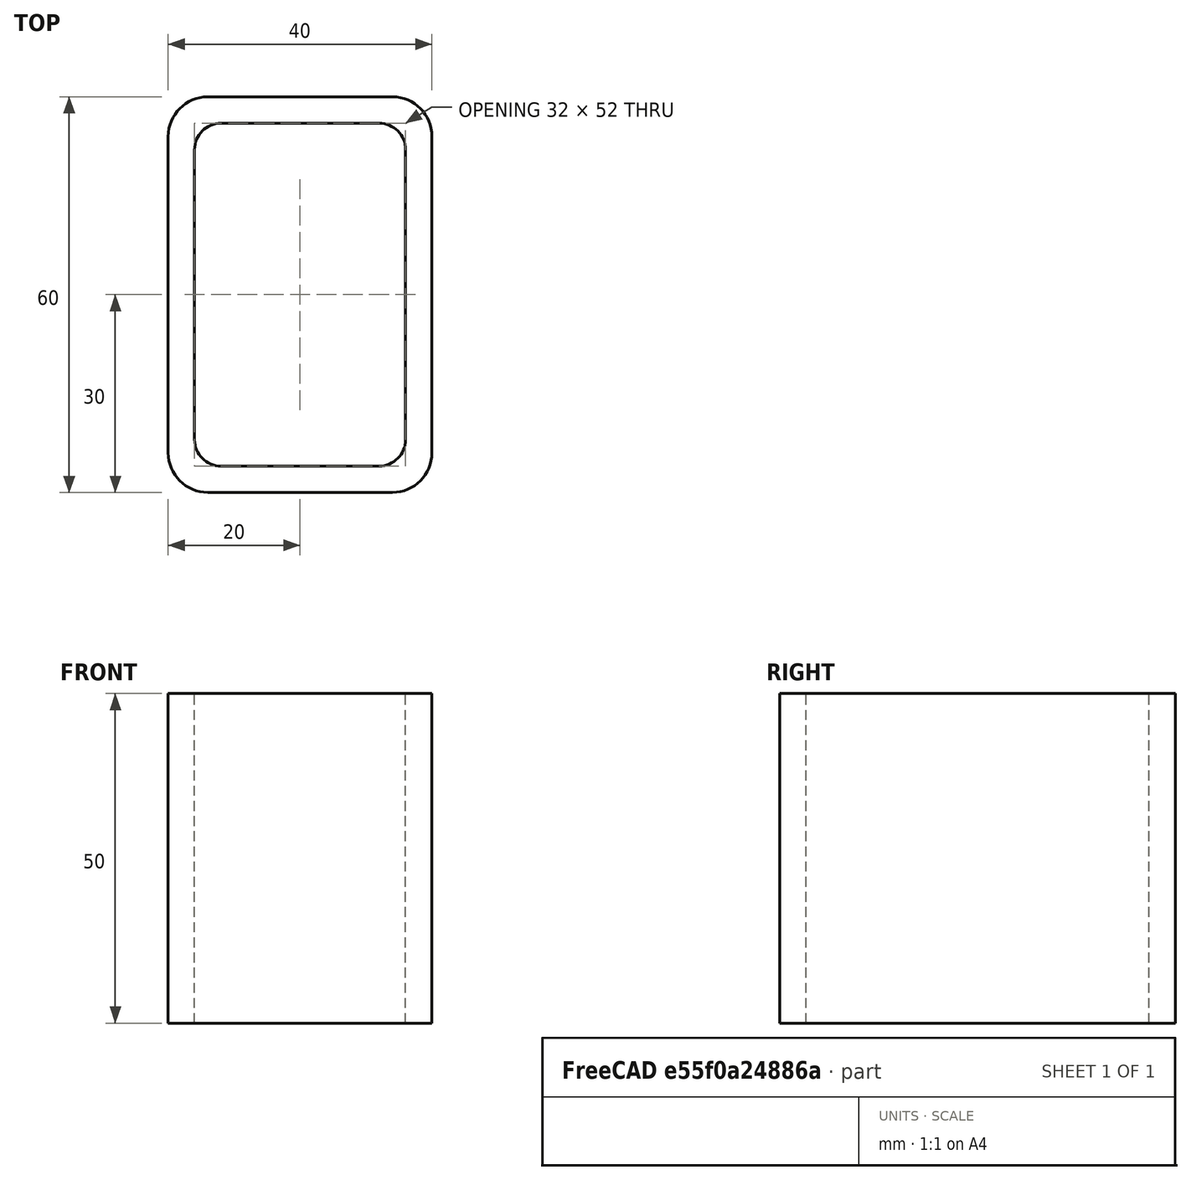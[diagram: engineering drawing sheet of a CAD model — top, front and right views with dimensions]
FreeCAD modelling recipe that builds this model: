
FCSTD DOCUMENT  (FreeCAD 0.15R4671 (Git))
Label: Rectangular hollow section 60x40x4 EN10219 S235JRH
License: All rights reserved
LicenseURL: http://en.wikipedia.org/wiki/All_rights_reserved
objects: Sketcher::SketchObject×1, Part::Extrusion×1
note: 2 computed .brp shape members not serialized (recipe doc carries the construction recipe); baked Part::Feature solids carry a one-line shape summary decoded from their .brp

FEATURE [Sketcher::SketchObject] Sketch
  sketch-geometry (16):
    g0: LineSegment StartX=-12 StartY=26 StartZ=0 EndX=12 EndY=26 EndZ=0
    g1: LineSegment StartX=16 StartY=22 StartZ=0 EndX=16 EndY=-22 EndZ=0
    g2: LineSegment StartX=12 StartY=-26 StartZ=0 EndX=-12 EndY=-26 EndZ=0
    g3: LineSegment StartX=-16 StartY=-22 StartZ=0 EndX=-16 EndY=22 EndZ=0
    g4: LineSegment StartX=-14 StartY=30 StartZ=0 EndX=14 EndY=30 EndZ=0
    g5: LineSegment StartX=20 StartY=24 StartZ=0 EndX=20 EndY=-24 EndZ=0
    g6: LineSegment StartX=14 StartY=-30 StartZ=0 EndX=-14 EndY=-30 EndZ=0
    g7: LineSegment StartX=-20 StartY=-24 StartZ=0 EndX=-20 EndY=24 EndZ=0
    g8: ArcOfCircle CenterX=-12 CenterY=22 CenterZ=0 NormalX=0 NormalY=0 NormalZ=1 Radius=4 StartAngle=1.5708 EndAngle=3.14159
    g9: ArcOfCircle CenterX=12 CenterY=22 CenterZ=0 NormalX=0 NormalY=0 NormalZ=1 Radius=4 StartAngle=0 EndAngle=1.5708
    g10: ArcOfCircle CenterX=12 CenterY=-22 CenterZ=0 NormalX=0 NormalY=0 NormalZ=1 Radius=4 StartAngle=4.71239 EndAngle=6.28319
    g11: ArcOfCircle CenterX=-12 CenterY=-22 CenterZ=0 NormalX=0 NormalY=0 NormalZ=1 Radius=4 StartAngle=3.14159 EndAngle=4.71239
    g12: ArcOfCircle CenterX=14 CenterY=24 CenterZ=0 NormalX=0 NormalY=0 NormalZ=1 Radius=6 StartAngle=0 EndAngle=1.5708
    g13: ArcOfCircle CenterX=14 CenterY=-24 CenterZ=0 NormalX=0 NormalY=0 NormalZ=1 Radius=6 StartAngle=4.71239 EndAngle=6.28319
    g14: ArcOfCircle CenterX=-14 CenterY=-24 CenterZ=0 NormalX=0 NormalY=0 NormalZ=1 Radius=6 StartAngle=3.14159 EndAngle=4.71239
    g15: ArcOfCircle CenterX=-14 CenterY=24 CenterZ=0 NormalX=0 NormalY=0 NormalZ=1 Radius=6 StartAngle=1.5708 EndAngle=3.14159
  constraints (36):
    c: Horizontal(g2)
    c: Vertical(g3)
    c: Horizontal(g6)
    c: Vertical(g7)
    c: Tangent(g3,g8) = 1.5708
    c: Tangent(g0,g8) = 1.5708
    c: Tangent(g0,g9) = 1.5708
    c: Tangent(g1,g9) = 1.5708
    c: Tangent(g1,g10) = 1.5708
    c: Tangent(g2,g10) = 1.5708
    c: Tangent(g2,g11) = 1.5708
    c: Tangent(g3,g11) = 1.5708
    c: Tangent(g4,g12) = 1.5708
    c: Tangent(g5,g12) = 1.5708
    c: Tangent(g5,g13) = 1.5708
    c: Tangent(g6,g13) = 1.5708
    c: Tangent(g6,g14) = 1.5708
    c: Tangent(g7,g14) = 1.5708
    c: Tangent(g7,g15) = 1.5708
    c: Tangent(g4,g15) = 1.5708
    c: Equal(g9,g8)
    c: Equal(g9,g11)
    c: Equal(g9,g10)
    c: Equal(g12,g15)
    c: Equal(g12,g14)
    c: Equal(g12,g13)
    c: Symmetric(g4,g6,g-1)
    c: Symmetric(g7,g5,g-2)
    c: DistanceY(g4,g6) = -60
    c: DistanceX(g7,g5) = 40
    c: Symmetric(g3,g1,g-2)
    c: Symmetric(g0,g2,g-1)
    c: DistanceY(g0,g4) = 4
    c: DistanceX(g5,g1) = -4
    c: Radius(g9) = 4
    c: Radius(g12) = 6
FEATURE [Part::Extrusion] Extrude  label="Rectangular hollow section 60x40x4 EN10219 S235JRH"
  Base = -> Sketch
  Dir = (0,0,50)
  Solid = true
